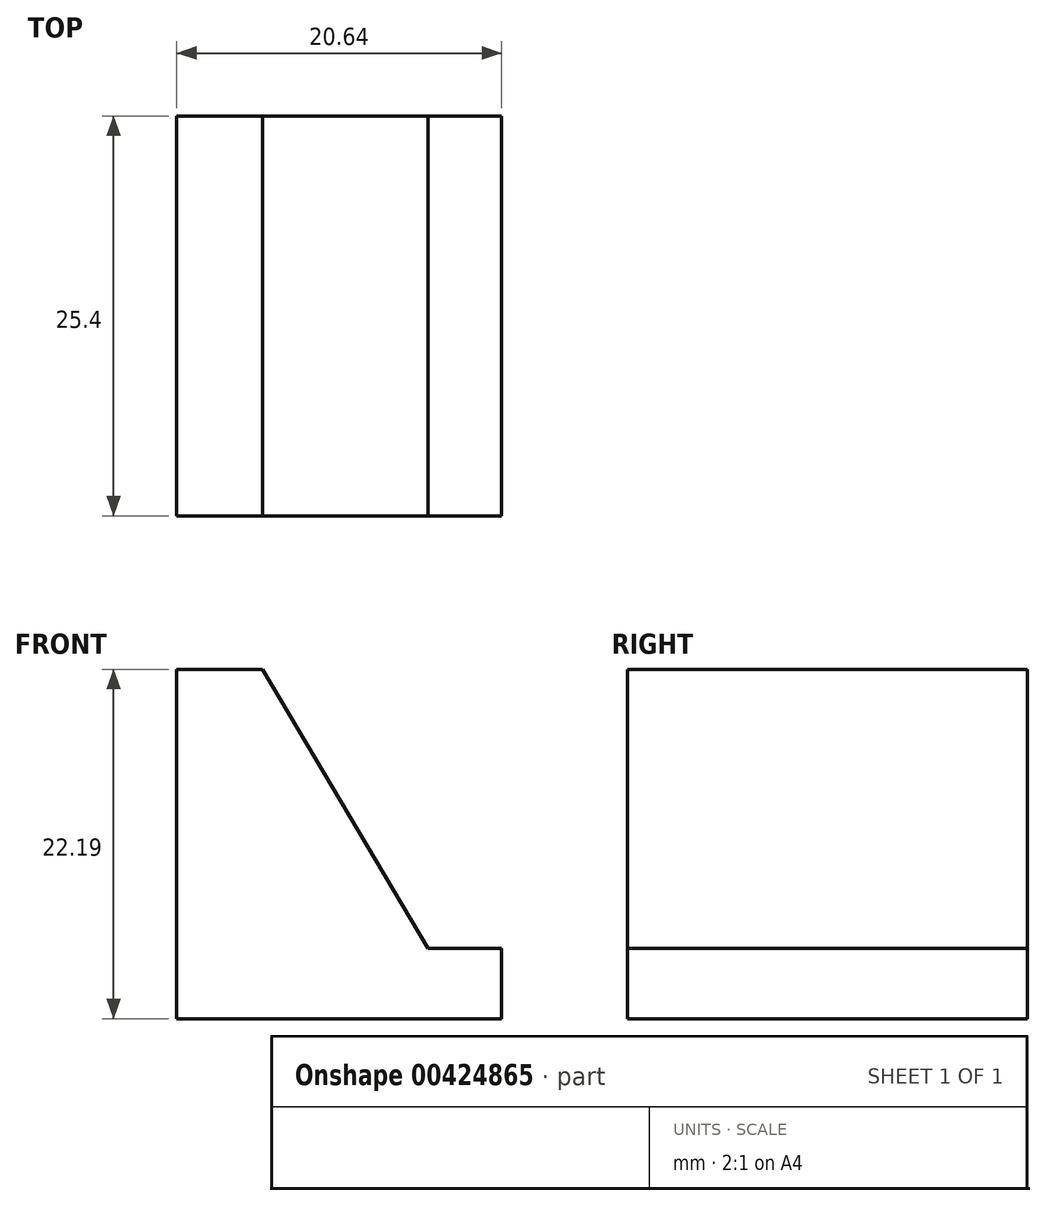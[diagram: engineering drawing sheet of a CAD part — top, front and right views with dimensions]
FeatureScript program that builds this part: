
annotation { "Feature Type Name" : "Feature", "Feature Type Description" : "" }
export const myFeature = defineFeature(function(context is Context, id is Id, definition is map)
    precondition{}
    {
        {
            var Q0;
            Q0=qCreatedBy(makeId("Front.planeOp"),FACE);
            var sketch = newSketch(context, id + "F0", { "sketchPlane" : qUnion([Q0])});
            skLineSegment(sketch, "E0", {"start": v(0, 0) * mm, "end": v(20.64, 0) * mm});
            skLineSegment(sketch, "E1", {"start": v(0, 0) * mm, "end": v(0, 22.2) * mm});
            skLineSegment(sketch, "E2", {"start": v(0, 22.2) * mm, "end": v(5.45, 22.2) * mm});
            skLineSegment(sketch, "E3", {"start": v(20.64, 0) * mm, "end": v(20.64, 4.48) * mm});
            skLineSegment(sketch, "E4", {"start": v(20.64, 4.48) * mm, "end": v(15.96, 4.48) * mm});
            skLineSegment(sketch, "E5", {"start": v(5.45, 22.2) * mm, "end": v(15.96, 4.48) * mm});
            skSolve(sketch);
        }
        {
            var Q0;
            Q0=makeQuery(id+"F0.imprint","IMPRINT",FACE,{"disambiguationData":[TD([[makeQuery(id+"F0.imprint","IMPRINT",EDGE,{"derivedFrom":sQuery(id+"F0.wireOp",EDGE,"E0")}),1.0]])]});
            extrude(context, id + "F1", {"entities" : qUnion([Q0]), "depth" : 25.4 * mm});
        }
    });
